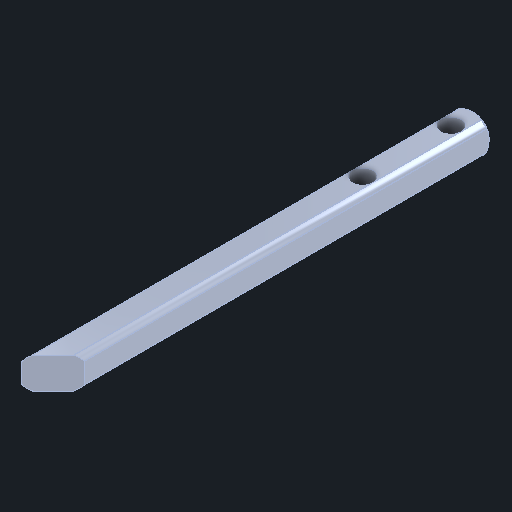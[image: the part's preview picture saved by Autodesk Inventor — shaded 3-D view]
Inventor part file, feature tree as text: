
AUTODESK INVENTOR PART (.ipt)
format: ipt  version: 2025 (Build 290162000, 162)  size: 188,928 bytes
history: native  units: in
note: dims shown in document units (in); Inventor stores cm internally (conversion verified against a paired STEP export)
features: extrude x4, sketch x4, thicken_offset x1, other x1
ambient origin geometry x8: Origin, YZ Plane, XZ Plane, XY Plane, X Axis, Y Axis, Z Axis, Center Point
bodies: Solid1 (feature_tree)
feature tree (10):
  extrude  "Extrusion1"  Depth=12.1875in
  thicken_offset  "Thicken1"
  extrude  "Extrusion2"  Depth=20.625in
  extrude  "Extrusion3"  Depth=0.165in
  extrude  "Extrusion4"  Depth=0.3084in
  sketch  "Sketch2"  dims[d0=0.0625in d1=0.0in d2=12.1875in]
  sketch  "Sketch3"  dims[d3=12.125in d4=20.625in]
  sketch  "Sketch4"  dims[d5=0.0in d6=0.165in]
  sketch  "Sketch5"  dims[d8=1.0in d9=0.0in d10=0.3084in d11=1.0in d12=0.0in d13=0.165in]
  other  "Cut-Revolve3"
